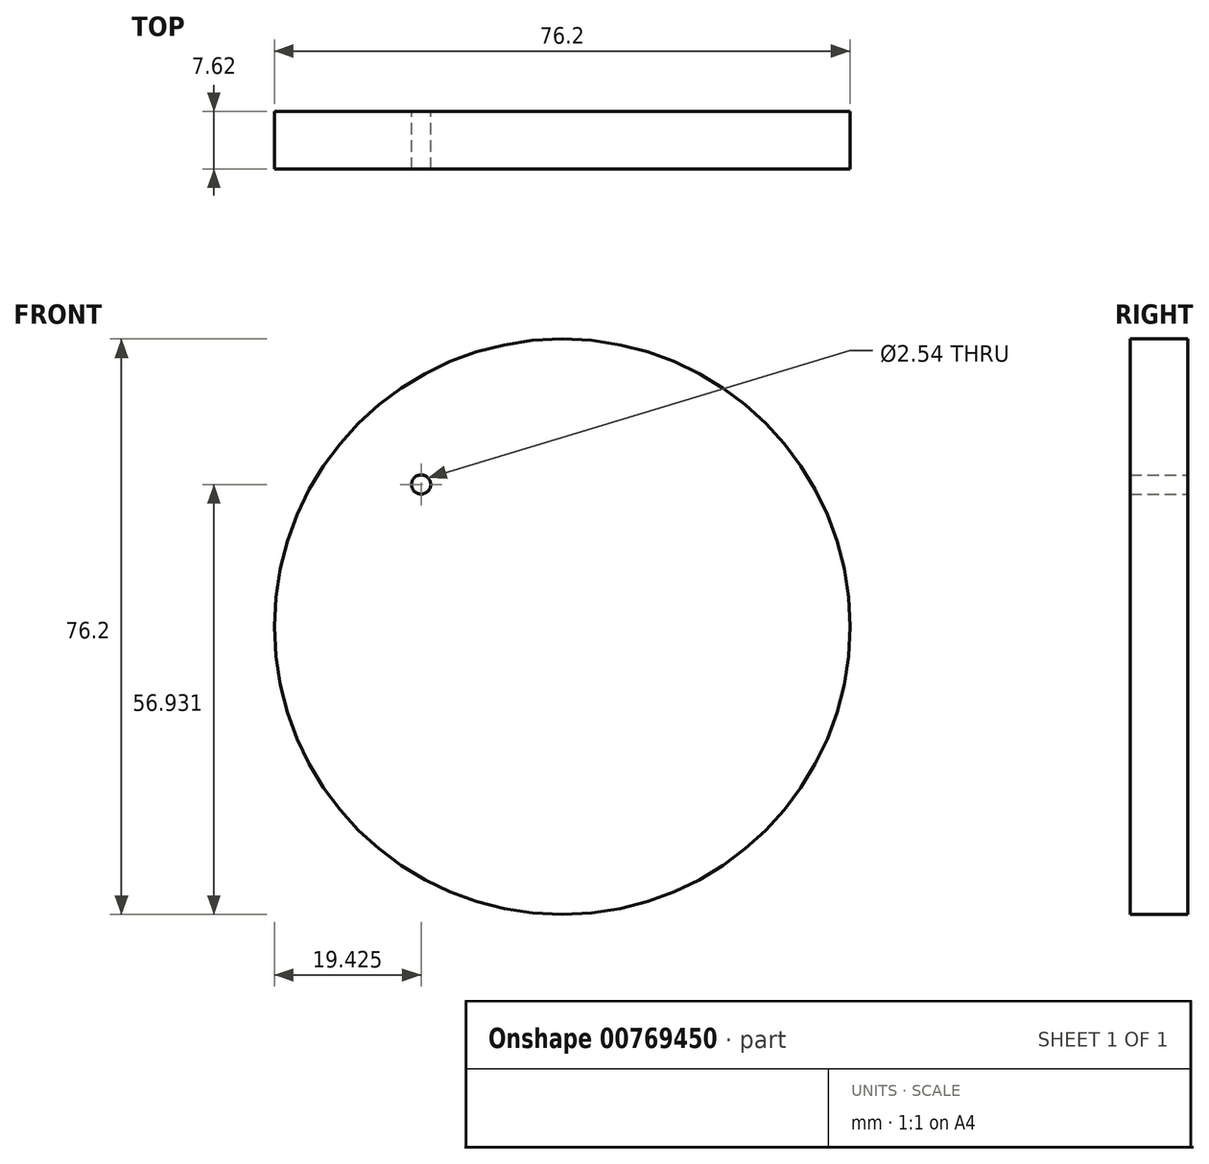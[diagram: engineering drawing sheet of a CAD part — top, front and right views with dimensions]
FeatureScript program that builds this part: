
annotation { "Feature Type Name" : "Feature", "Feature Type Description" : "" }
export const myFeature = defineFeature(function(context is Context, id is Id, definition is map)
    precondition{}
    {
        {
            var Q0;
            Q0=qCreatedBy(makeId("Front.planeOp"),FACE);
            var sketch = newSketch(context, id + "F0", { "sketchPlane" : qUnion([Q0])});
            skCircle(sketch, "E0", {"center": v(0, 0) * mm, "radius": 38.1 * mm});
            skSolve(sketch);
        }
        {
            var Q0;
            Q0=makeQuery(id+"F0.imprint","IMPRINT",FACE,{"disambiguationData":[TD([[makeQuery(id+"F0.imprint","IMPRINT",EDGE,{"derivedFrom":sQuery(id+"F0.wireOp",EDGE,"E0")}),1.0]])]});
            var sketch = newSketch(context, id + "F1", { "sketchPlane" : qUnion([Q0])});
            skPoint(sketch, "E1", {"position": v(-18.67, 18.83) * mm});
            skSolve(sketch);
        }
        {
            var Q0;
            Q0=makeQuery(id+"F0.imprint","IMPRINT",FACE,{"disambiguationData":[TD([[makeQuery(id+"F0.imprint","IMPRINT",EDGE,{"derivedFrom":sQuery(id+"F0.wireOp",EDGE,"E0")}),1.0]])]});
            extrude(context, id + "F2", {"entities" : qUnion([Q0]), "depth" : 7.62 * mm, "offsetDistance" : 25.4 * mm});
        }
        {
            var Q0;
            Q0=sQuery(id+"F1.wireOp",VERTEX,"E1");
            var Q1;
            Q1=makeQuery(id+"F2.opExtrude","SWEPT_BODY",BODY,{"disambiguationData":[OSD([sQuery(id+"F0.wireOp",EDGE,"E0")])]});
            hole(context, id + "F3", {"style" : HoleStyle.SIMPLE, "endStyle" : HoleEndStyle.THROUGH, "oppositeDirection" : true, "holeDiameter" : 2.54 * mm, "majorDiameter" : 6.35 * mm, "isTappedThrough" : true, "tappedDepth" : 12.7 * mm, "tapClearance" : 3, "locations" : qUnion([Q0]), "scope" : qUnion([Q1])});
        }
    });
